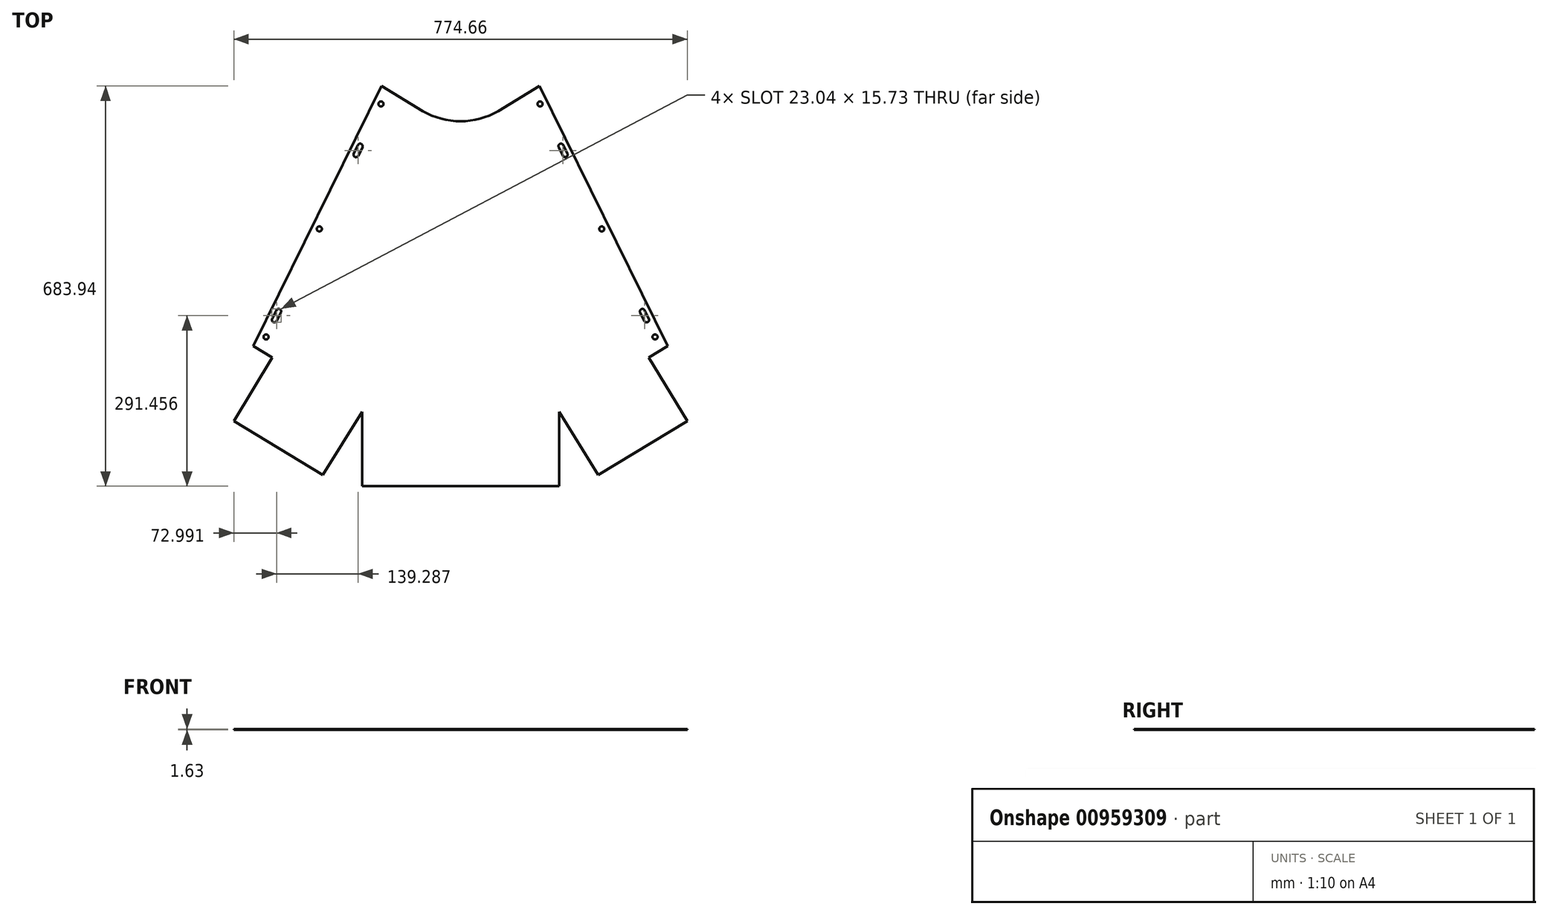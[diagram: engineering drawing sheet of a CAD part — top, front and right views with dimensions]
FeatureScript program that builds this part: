
annotation { "Feature Type Name" : "Feature", "Feature Type Description" : "" }
export const myFeature = defineFeature(function(context is Context, id is Id, definition is map)
    precondition{}
    {
        {
            var Q0;
            Q0=qCreatedBy(makeId("Top.planeOp"),FACE);
            var sketch = newSketch(context, id + "F0", { "sketchPlane" : qUnion([Q0])});
            skLineSegment(sketch, "E0", {"start": v(-134.94, 0) * mm, "end": v(134.94, 0) * mm});
            skLineSegment(sketch, "E1", {"start": v(-134.94, 0) * mm, "end": v(-354.01, -444.22) * mm});
            skLineSegment(sketch, "E2", {"start": v(0, 0) * mm, "end": v(0, -416.22) * mm});
            skLineSegment(sketch, "E3", {"start": v(-354.01, -444.22) * mm, "end": v(-321.44, -463.98) * mm});
            skLineSegment(sketch, "E4", {"start": v(-321.44, -463.98) * mm, "end": v(-387.33, -572.55) * mm});
            skLineSegment(sketch, "E5", {"start": v(-387.33, -572.55) * mm, "end": v(-235.33, -664.8) * mm});
            skLineSegment(sketch, "E6", {"start": v(-235.33, -664.8) * mm, "end": v(-168.27, -556.94) * mm});
            skLineSegment(sketch, "E7", {"start": v(-168.27, -556.94) * mm, "end": v(-168.27, -683.94) * mm});
            skLineSegment(sketch, "E8.MirrorCS", {"start": v(134.94, 0) * mm, "end": v(354.01, -444.22) * mm});
            skPoint(sketch, "E9", {"position": v(0, -60.33) * mm});
            skLineSegment(sketch, "E10", {"start": v(-425.96, -215.27) * mm, "end": v(-527.48, -349.47) * mm});
            skLineSegment(sketch, "E11", {"start": v(0, -416.22) * mm, "end": v(0, -689.44) * mm});
            skLineSegment(sketch, "E12", {"start": v(-168.27, -683.94) * mm, "end": v(0, -683.94) * mm});
            skLineSegment(sketch, "E13.MirrorCS", {"start": v(354.01, -444.22) * mm, "end": v(321.44, -463.98) * mm});
            skLineSegment(sketch, "E14.MirrorCS", {"start": v(321.44, -463.98) * mm, "end": v(387.33, -572.55) * mm});
            skLineSegment(sketch, "E15.MirrorCS", {"start": v(387.33, -572.55) * mm, "end": v(235.33, -664.8) * mm});
            skLineSegment(sketch, "E16.MirrorCS", {"start": v(235.33, -664.8) * mm, "end": v(168.28, -556.94) * mm});
            skLineSegment(sketch, "E17.MirrorCS", {"start": v(168.28, -556.94) * mm, "end": v(168.28, -683.94) * mm});
            skLineSegment(sketch, "E18.MirrorCS", {"start": v(168.28, -683.94) * mm, "end": v(0, -683.94) * mm});
            skCircle(sketch, "E19", {"center": v(-135.9, -30.68) * mm, "radius": 4.32 * mm});
            skCircle(sketch, "E20", {"center": v(-241.24, -244.26) * mm, "radius": 4.32 * mm});
            skCircle(sketch, "E21", {"center": v(-332.28, -428.85) * mm, "radius": 4.32 * mm});
            skArc(sketch, "E22", {"start": v(-167.62, -104.75) * mm, "mid": v(-169.59, -98.97) * mm, "end": v(-175.37, -100.93) * mm});
            skArc(sketch, "E23", {"start": v(-321.77, -397.78) * mm, "mid": v(-319.8, -403.57) * mm, "end": v(-314.02, -401.6) * mm});
            skLineSegment(sketch, "E24", {"start": v(-135.9, -30.68) * mm, "end": v(-147.3, -25.06) * mm});
            skArc(sketch, "E25", {"start": v(-182.48, -115.35) * mm, "mid": v(-180.52, -121.14) * mm, "end": v(-174.74, -119.17) * mm});
            skArc(sketch, "E26", {"start": v(-306.91, -387.18) * mm, "mid": v(-308.87, -381.4) * mm, "end": v(-314.66, -383.36) * mm});
            skLineSegment(sketch, "E27", {"start": v(-174.74, -119.17) * mm, "end": v(-167.62, -104.75) * mm});
            skLineSegment(sketch, "E28", {"start": v(-314.02, -401.6) * mm, "end": v(-306.91, -387.18) * mm});
            skLineSegment(sketch, "E29.0", {"start": v(-182.48, -115.35) * mm, "end": v(-175.37, -100.93) * mm});
            skLineSegment(sketch, "E30.0", {"start": v(-321.77, -397.78) * mm, "end": v(-314.66, -383.36) * mm});
            skCircle(sketch, "E31.MirrorC", {"center": v(332.28, -428.85) * mm, "radius": 4.32 * mm});
            skArc(sketch, "E32.MirrorCS", {"start": v(321.77, -397.78) * mm, "mid": v(319.8, -403.57) * mm, "end": v(314.02, -401.6) * mm});
            skLineSegment(sketch, "E33.MirrorCS", {"start": v(314.02, -401.6) * mm, "end": v(306.91, -387.18) * mm});
            skLineSegment(sketch, "E34.MirrorCS", {"start": v(321.77, -397.78) * mm, "end": v(314.66, -383.36) * mm});
            skArc(sketch, "E35.MirrorCS", {"start": v(306.91, -387.18) * mm, "mid": v(308.87, -381.4) * mm, "end": v(314.66, -383.36) * mm});
            skCircle(sketch, "E36.MirrorC", {"center": v(241.24, -244.26) * mm, "radius": 4.32 * mm});
            skLineSegment(sketch, "E37.MirrorCS", {"start": v(174.74, -119.17) * mm, "end": v(167.62, -104.75) * mm});
            skArc(sketch, "E38.MirrorCS", {"start": v(167.62, -104.75) * mm, "mid": v(169.59, -98.97) * mm, "end": v(175.37, -100.93) * mm});
            skLineSegment(sketch, "E39.MirrorCS", {"start": v(182.48, -115.35) * mm, "end": v(175.37, -100.93) * mm});
            skArc(sketch, "E40.MirrorCS", {"start": v(182.48, -115.35) * mm, "mid": v(180.52, -121.14) * mm, "end": v(174.74, -119.17) * mm});
            skCircle(sketch, "E41.MirrorC", {"center": v(135.9, -30.68) * mm, "radius": 4.32 * mm});
            skLineSegment(sketch, "E42", {"start": v(-134.94, 0) * mm, "end": v(-64.37, -42.83) * mm});
            skLineSegment(sketch, "E43.MirrorCS", {"start": v(134.94, 0) * mm, "end": v(64.37, -42.83) * mm});
            skArc(sketch, "E44", {"start": v(-64.37, -42.83) * mm, "mid": v(0, -60.33) * mm, "end": v(64.37, -42.83) * mm});
            skLineSegment(sketch, "E45", {"start": v(135.9, -30.68) * mm, "end": v(147.3, -25.06) * mm});
            skSolve(sketch);
        }
        {
            var Q0;
            {var subQ1=sQuery(id+"F0.wireOp",EDGE,"E3");Q0=makeQuery(id+"F0.imprint","IMPRINT",FACE,{"disambiguationData":[TD([[makeQuery(id+"F0.imprint","IMPRINT",EDGE,{"derivedFrom":subQ1}),1.0]])]});}
            var Q1;
            Q1=makeQuery(id+"F0.imprint","IMPRINT",FACE,{"disambiguationData":[TD([[makeQuery(id+"F0.imprint","IMPRINT",EDGE,{"derivedFrom":sQuery(id+"F0.wireOp",EDGE,"E8.MirrorCS")}),-1.0]])]});
            extrude(context, id + "F1", {"entities" : qUnion([Q0, Q1]), "depth" : 1.63 * mm, "offsetDistance" : 25.4 * mm});
        }
    });
